# Revit family: QF_GIORIK_KHG061_KTG061_KHG061W_KTG061W
name_source: partatom
category: Specialty Equipment
revit_build: Autodesk Revit 2014 (Build: 20140709_2115(x64)
units: mm (PartAtom-declared; Revit-internal decimal feet)

## types (4) — shared parameters
Assembly Code = E1090320
Cold Water Connection Height = 98 mm  [stored 0.321522 ft]
Cold Water Size = 1"
Cold Water Temperature Recommended = 0 °C
Cycle = 50 Hz
FL Amps = 0 A
Gas Connection Height = 714 mm  [stored 2.34252 ft]
Gas Input = 5500 W
Gas KW = 5.5
Gas Size = 1"
HP = 0
Indirect Waste Connection Height = 89 mm  [stored 0.291995 ft]
Indirect Waste Flow = 0.0 L/s
Indirect Waste Size = 1 1/2"
Manufacturer = GIORIK
Max Overcurrent Protection = 16 A
Min Ckt Ampacity = 0 A
Phase = 1
Touch screen control = Yes
URL = www.giorik.com
Volts = 230 V
Waste Water Discharge Temperature = 0 °C
Weight in Pounds = 211.644

## per-type parameters (varying)
| type | Apparent Power | Description | Watts |
| KHG061 | 1300 VA | GAS OVEN 6 GN 1/1 COMBINED CONVECTION/STEAM TOUCH SCREEN CONTROL - HIGH EFFICIENCY BOILER VERSION | 1300 W |
| KTG061 | 300 VA | GAS OVEN 6 GN 1/1 COMBINED CONVECTION/STEAM TOUCH SCREEN CONTROL - DIRECT STEAM VERSION | 300 W |
| KHG061W | 1300 VA | GAS OVEN 6 GN 1/1 COMBINED CONVECTION/STEAM TOUCH SCREEN CONTROL - HIGH EFFICIENCY BOILER VERSION | 1300 W |
| KTG061W | 300 VA | GAS OVEN 6 GN 1/1 COMBINED CONVECTION/STEAM TOUCH SCREEN CONTROL - DIRECT STEAM VERSION | 300 W |

note: column(s) folded — value = type name in every type: Model

note: [stored X ft] marks values corroborated as IEEE doubles in the binary element streams (Revit-internal decimal feet)

## geometry (parser evidence)
native form markers: Blend x7, Sweep x1
no freeform markers — native parametric forms only
